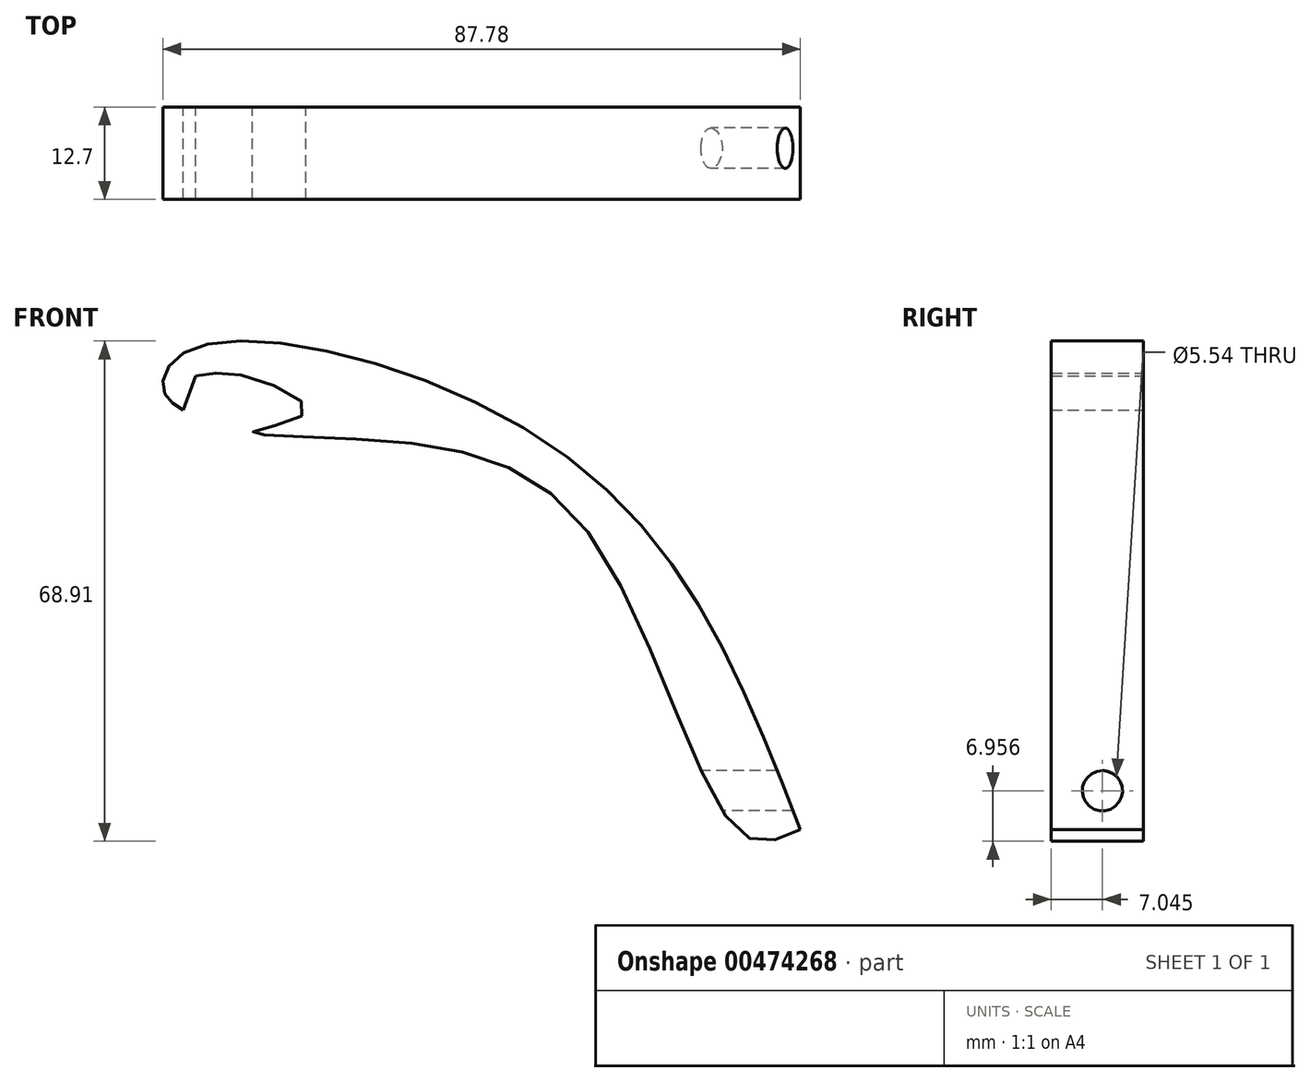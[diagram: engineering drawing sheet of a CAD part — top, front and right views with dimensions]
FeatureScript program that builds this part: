
annotation { "Feature Type Name" : "Feature", "Feature Type Description" : "" }
export const myFeature = defineFeature(function(context is Context, id is Id, definition is map)
    precondition{}
    {
        {
            var Q0;
            Q0=qCreatedBy(makeId("Front.planeOp"),FACE);
            var sketch = newSketch(context, id + "F0", { "sketchPlane" : qUnion([Q0])});
            skFitSpline(sketch, "E0", {"points": [v(63.22, -21.73) * mm, v(30.13, 30.38) * mm, v(-20.75, 44.45) * mm, v(-24.45, 38.77) * mm, v(-21.73, 36.06) * mm], "startDerivative": vector(-56.91, 147.65) * mm, "endDerivative": vector(35.68, -21.87) * mm});
            skLineSegment(sketch, "E1", {"start": v(-21.73, 36.06) * mm, "end": v(-20, 40.75) * mm});
            skFitSpline(sketch, "E2", {"points": [v(-20, 40.75) * mm, v(-13.09, 40.75) * mm, v(-4.94, 35.81) * mm, v(-12.1, 33.1) * mm, v(5.43, 31.86) * mm, v(34.33, 18.77) * mm, v(55.07, -22.23) * mm, v(63.22, -21.73) * mm], "startDerivative": vector(60.68, 11.98) * mm, "endDerivative": vector(80.87, 37.72) * mm});
            skSolve(sketch);
        }
        {
            var Q0;
            Q0=makeQuery(id+"F0.imprint","IMPRINT",FACE,{"disambiguationData":[TD([[makeQuery(id+"F0.imprint","IMPRINT",EDGE,{"derivedFrom":sQuery(id+"F0.wireOp",EDGE,"E0")}),1.0]])]});
            extrude(context, id + "F1", {"entities" : qUnion([Q0]), "depth" : 12.7 * mm});
        }
        {
            var Q0;
            Q0=qCreatedBy(makeId("Right.planeOp"),FACE);
            var sketch = newSketch(context, id + "F2", { "sketchPlane" : qUnion([Q0])});
            skCircle(sketch, "E3", {"center": v(-5.65, -16.36) * mm, "radius": 2.77 * mm});
            skSolve(sketch);
        }
        {
            var Q0;
            Q0=makeQuery(id+"F2.imprint","IMPRINT",FACE,{"disambiguationData":[TD([[makeQuery(id+"F2.imprint","IMPRINT",EDGE,{"derivedFrom":sQuery(id+"F2.wireOp",EDGE,"E3")}),1.0]])]});
            extrude(context, id + "F3", {"entities" : qUnion([Q0]), "operationType" : NewBodyOperationType.REMOVE, "depth" : 88.14 * mm});
        }
    });
